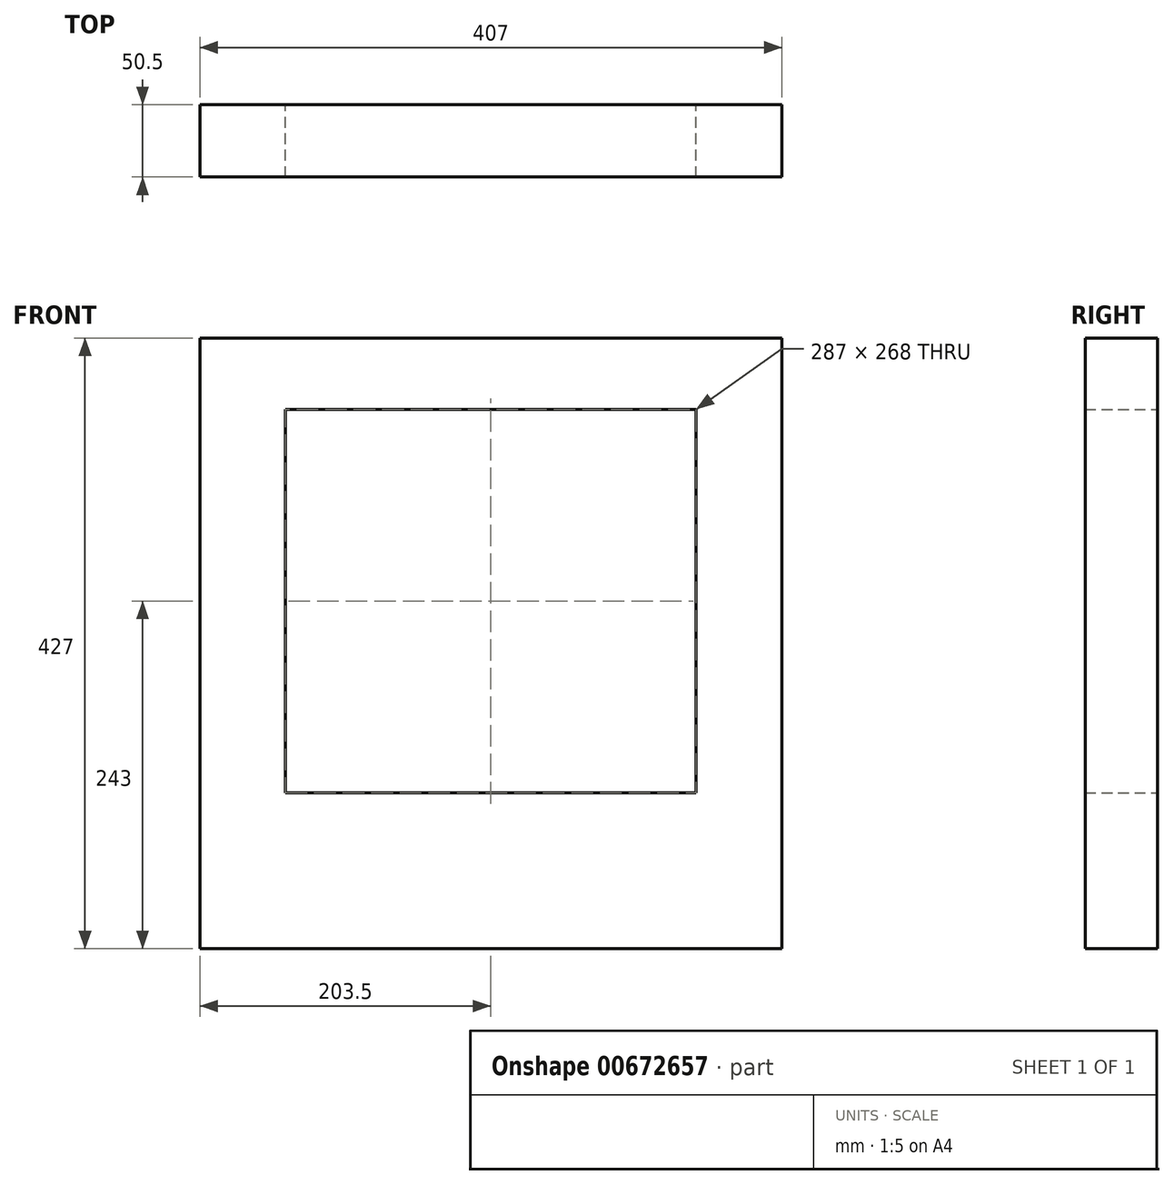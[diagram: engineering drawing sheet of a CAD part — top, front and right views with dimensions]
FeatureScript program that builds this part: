
annotation { "Feature Type Name" : "Feature", "Feature Type Description" : "" }
export const myFeature = defineFeature(function(context is Context, id is Id, definition is map)
    precondition{}
    {
        {
            var Q0;
            Q0=qCreatedBy(makeId("Front.planeOp"),FACE);
            var sketch = newSketch(context, id + "F0", { "sketchPlane" : qUnion([Q0])});
            skLineSegment(sketch, "E0.bottom", {"start": v(0, 0) * mm, "end": v(407, 0) * mm});
            skLineSegment(sketch, "E0.top", {"start": v(0, -427) * mm, "end": v(407, -427) * mm});
            skLineSegment(sketch, "E0.left", {"start": v(0, 0) * mm, "end": v(0, -427) * mm});
            skLineSegment(sketch, "E0.right", {"start": v(407, 0) * mm, "end": v(407, -427) * mm});
            skLineSegment(sketch, "E1.bottom", {"start": v(60, -50) * mm, "end": v(347, -50) * mm});
            skLineSegment(sketch, "E1.top", {"start": v(60, -318) * mm, "end": v(347, -318) * mm});
            skLineSegment(sketch, "E1.left", {"start": v(60, -50) * mm, "end": v(60, -318) * mm});
            skLineSegment(sketch, "E1.right", {"start": v(347, -50) * mm, "end": v(347, -318) * mm});
            skSolve(sketch);
        }
        {
            var Q0;
            Q0 = qSketchRegion(id + "F0", true);
            extrude(context, id + "F1", {"entities" : qUnion([Q0]), "depth" : 50.5 * mm, "offsetDistance" : 25 * mm});
        }
    });
